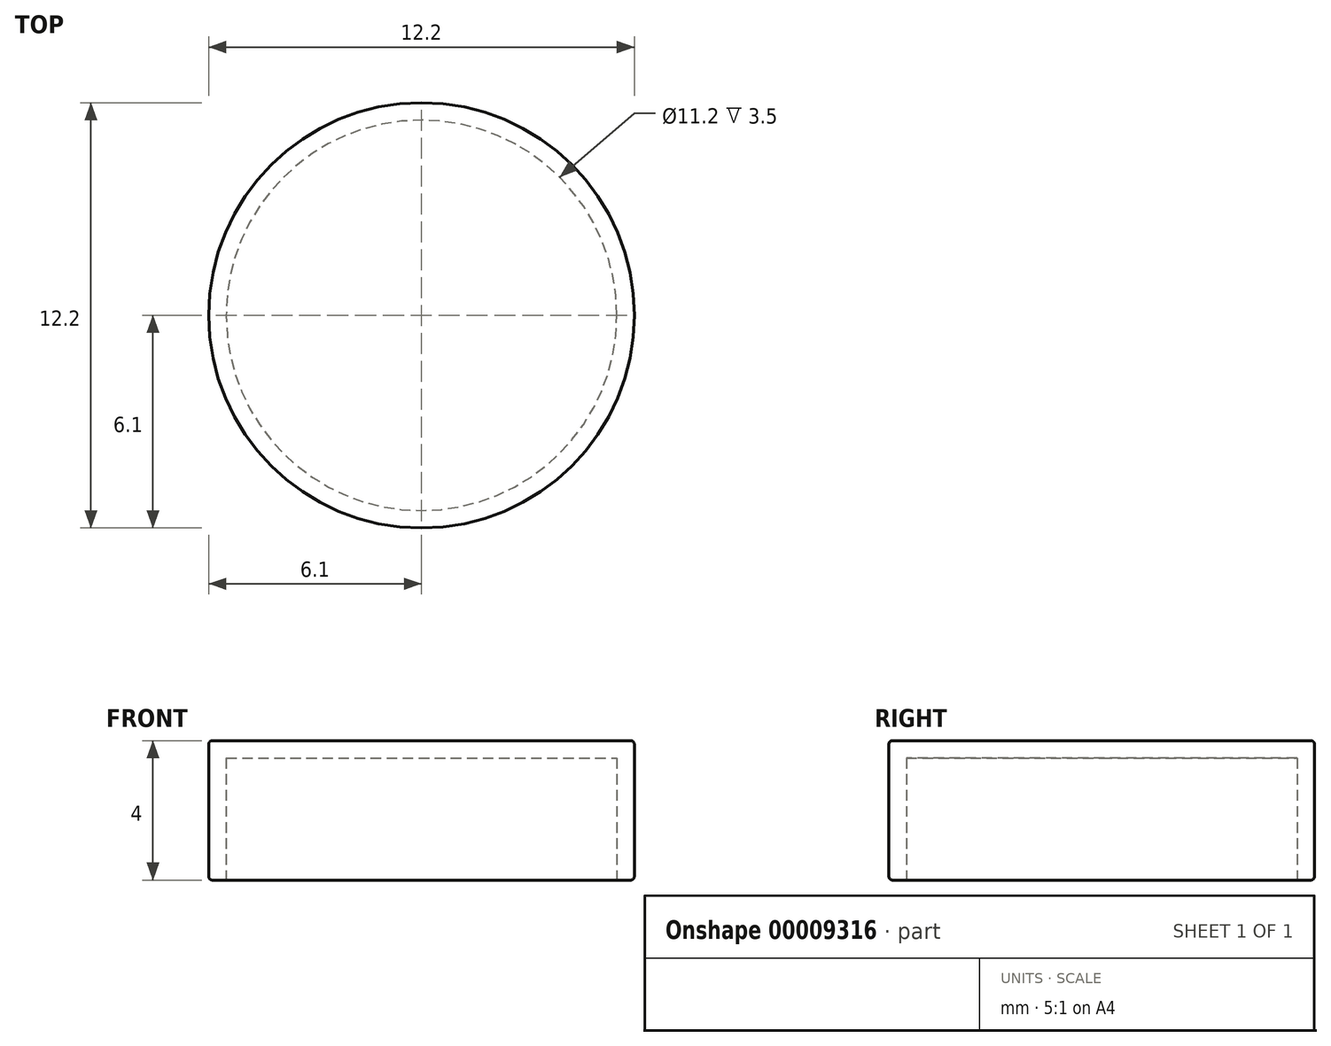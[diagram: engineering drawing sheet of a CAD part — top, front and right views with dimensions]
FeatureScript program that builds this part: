
annotation { "Feature Type Name" : "Feature", "Feature Type Description" : "" }
export const myFeature = defineFeature(function(context is Context, id is Id, definition is map)
    precondition{}
    {
        {
            var Q0;
            Q0=qCreatedBy(makeId("Right.planeOp"),FACE);
            var sketch = newSketch(context, id + "F0", { "sketchPlane" : qUnion([Q0])});
            skLineSegment(sketch, "E0", {"start": v(0, 0) * mm, "end": v(-9, 0) * mm});
            skLineSegment(sketch, "E1", {"start": v(-9, 0) * mm, "end": v(-9, 0.4) * mm});
            skLineSegment(sketch, "E2", {"start": v(-8.9, 0.5) * mm, "end": v(-6.1, 0.5) * mm});
            skLineSegment(sketch, "E3", {"start": v(0, 0.5) * mm, "end": v(0, 0) * mm});
            skLineSegment(sketch, "E4", {"start": v(-5.1, 0.5) * mm, "end": v(-5.1, 5.4) * mm});
            skLineSegment(sketch, "E5", {"start": v(-5.2, 5.5) * mm, "end": v(-5.5, 5.5) * mm});
            skLineSegment(sketch, "E6", {"start": v(-5.6, 5.4) * mm, "end": v(-5.6, 1) * mm});
            skPoint(sketch, "E7.newPointA", {"position": v(-5.6, 0.5) * mm});
            skPoint(sketch, "E7.newPointB", {"position": v(0, 0.5) * mm});
            skArc(sketch, "E7.filletArc", {"start": v(-6.1, 0.5) * mm, "mid": v(-5.75, 0.65) * mm, "end": v(-5.6, 1) * mm});
            skLineSegment(sketch, "E8", {"start": v(-5.1, 0.5) * mm, "end": v(0, 0.5) * mm});
            skPoint(sketch, "E9.visualSharp", {"position": v(-9, 0.5) * mm});
            skArc(sketch, "E9.filletArc", {"start": v(-8.9, 0.5) * mm, "mid": v(-8.97, 0.47) * mm, "end": v(-9, 0.4) * mm});
            skPoint(sketch, "E10.visualSharp", {"position": v(-5.6, 5.5) * mm});
            skArc(sketch, "E10.filletArc", {"start": v(-5.5, 5.5) * mm, "mid": v(-5.57, 5.47) * mm, "end": v(-5.6, 5.4) * mm});
            skPoint(sketch, "E11.visualSharp", {"position": v(-5.1, 5.5) * mm});
            skArc(sketch, "E11.filletArc", {"start": v(-5.1, 5.4) * mm, "mid": v(-5.13, 5.47) * mm, "end": v(-5.2, 5.5) * mm});
            skSolve(sketch);
        }
        {
            var Q0;
            Q0=makeQuery(id+"F0.imprint","IMPRINT",FACE,{"disambiguationData":[TD([[makeQuery(id+"F0.imprint","IMPRINT",EDGE,{"derivedFrom":sQuery(id+"F0.wireOp",EDGE,"E0")}),-1.0]])]});
            var sketch = newSketch(context, id + "F1", { "sketchPlane" : qUnion([Q0])});
            skLineSegment(sketch, "E12.0", {"start": v(-5.2, 5.5) * mm, "end": v(-5.5, 5.5) * mm, "construction": true});
            skLineSegment(sketch, "E13", {"start": v(0, 5.5) * mm, "end": v(0, 6) * mm});
            skLineSegment(sketch, "E14", {"start": v(0, 6) * mm, "end": v(-6, 6) * mm});
            skLineSegment(sketch, "E15", {"start": v(-6.1, 5.9) * mm, "end": v(-6.1, 2.1) * mm});
            skLineSegment(sketch, "E16", {"start": v(-5.6, 5.5) * mm, "end": v(0, 5.5) * mm});
            skLineSegment(sketch, "E17", {"start": v(-5.6, 5.5) * mm, "end": v(-5.6, 2) * mm});
            skLineSegment(sketch, "E18", {"start": v(-5.6, 2) * mm, "end": v(-6, 2) * mm});
            skPoint(sketch, "E19.visualSharp", {"position": v(-6.1, 6) * mm});
            skArc(sketch, "E19.filletArc", {"start": v(-6, 6) * mm, "mid": v(-6.07, 5.97) * mm, "end": v(-6.1, 5.9) * mm});
            skPoint(sketch, "E20.visualSharp", {"position": v(-6.1, 2) * mm});
            skArc(sketch, "E20.filletArc", {"start": v(-6.1, 2.1) * mm, "mid": v(-6.07, 2.03) * mm, "end": v(-6, 2) * mm});
            skSolve(sketch);
        }
        {
            var Q0;
            Q0=makeQuery(id+"F0.imprint","IMPRINT",FACE,{"disambiguationData":[TD([[makeQuery(id+"F0.imprint","IMPRINT",EDGE,{"derivedFrom":sQuery(id+"F0.wireOp",EDGE,"E0")}),-1.0]])]});
            var Q1;
            Q1=sQuery(id+"F0.wireOp",EDGE,"E3");
            revolve(context, id + "F2", {"entities" : qUnion([Q0]), "axis" : qUnion([Q1]), "revolveType" : RevolveType.FULL});
        }
        {
            var Q0;
            {var subQ7=sQuery(id+"F1.wireOp",EDGE,"E13");Q0=makeQuery(id+"F1.imprint","IMPRINT",FACE,{"disambiguationData":[TD([[makeQuery(id+"F1.imprint","IMPRINT",EDGE,{"derivedFrom":subQ7}),1.0]])]});}
            var Q1;
            Q1=sQuery(id+"F1.wireOp",EDGE,"E13");
            revolve(context, id + "F3", {"entities" : qUnion([Q0]), "axis" : qUnion([Q1]), "revolveType" : RevolveType.FULL});
        }
        {
            var Q0;
            Q0=makeQuery(id+"F2.opRevolve","SWEPT_BODY",BODY,{"disambiguationData":[OSD([sQuery(id+"F0.wireOp",EDGE,"E0"),sQuery(id+"F0.wireOp",EDGE,"E1"),sQuery(id+"F0.wireOp",EDGE,"E2"),sQuery(id+"F0.wireOp",EDGE,"E3"),sQuery(id+"F0.wireOp",EDGE,"E4"),sQuery(id+"F0.wireOp",EDGE,"E5"),sQuery(id+"F0.wireOp",EDGE,"E6"),sQuery(id+"F0.wireOp",EDGE,"E7.filletArc"),sQuery(id+"F0.wireOp",EDGE,"E8"),sQuery(id+"F0.wireOp",EDGE,"E9.filletArc"),sQuery(id+"F0.wireOp",EDGE,"E10.filletArc"),sQuery(id+"F0.wireOp",EDGE,"E11.filletArc")])]});
            deleteBodies(context, id + "F4", {"entities" : qUnion([Q0])});
        }
    });
